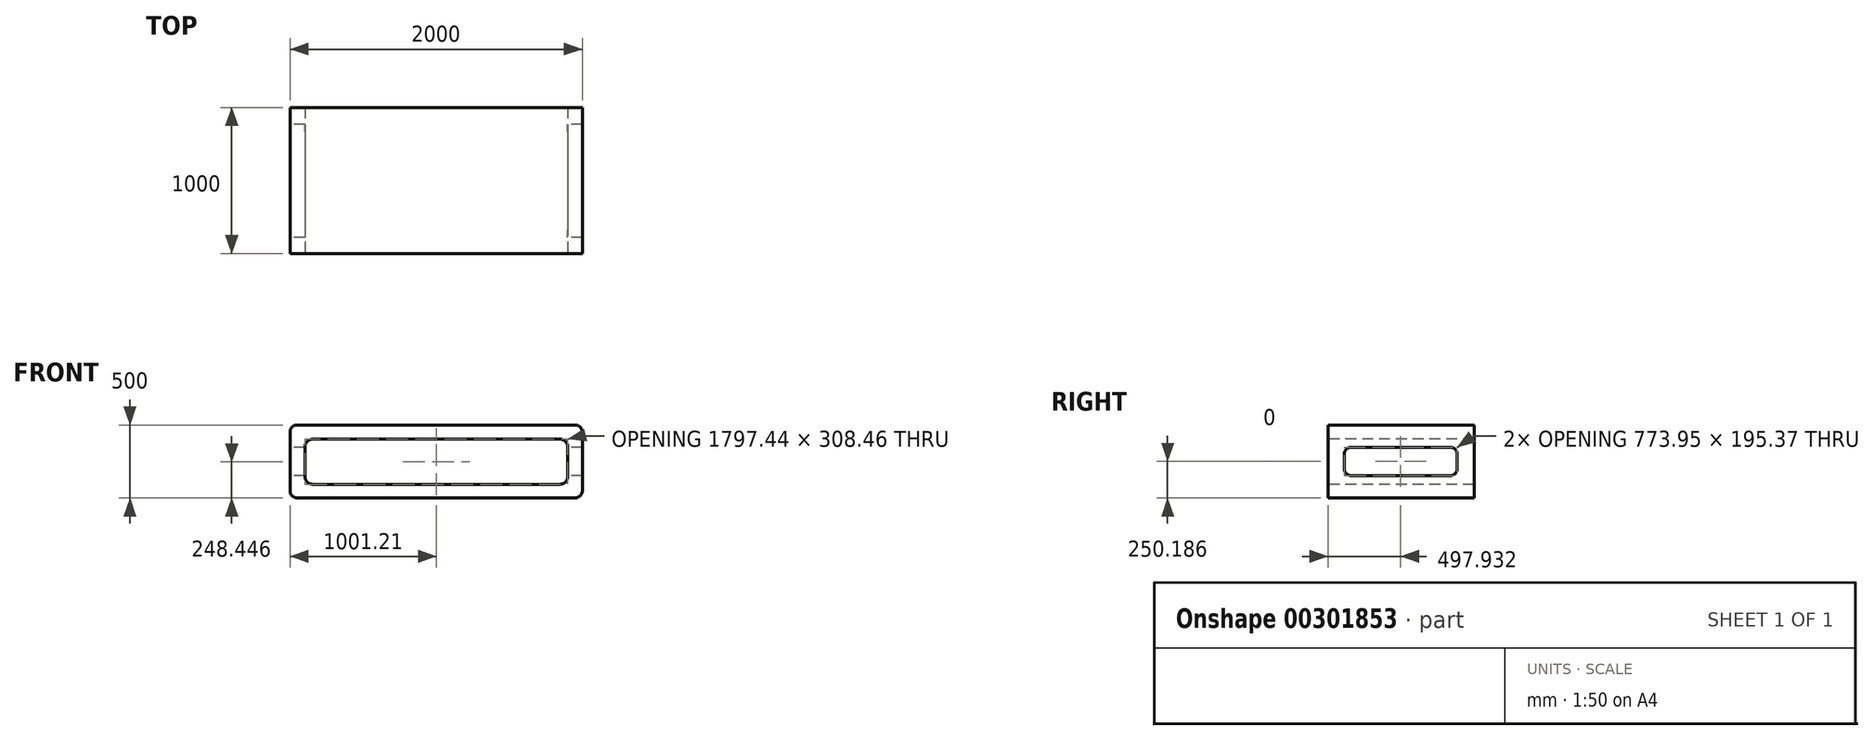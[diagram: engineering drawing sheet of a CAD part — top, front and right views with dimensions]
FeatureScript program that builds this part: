
annotation { "Feature Type Name" : "Feature", "Feature Type Description" : "" }
export const myFeature = defineFeature(function(context is Context, id is Id, definition is map)
    precondition{}
    {
        {
            var Q0;
            Q0=qCreatedBy(makeId("Front.planeOp"),FACE);
            var sketch = newSketch(context, id + "F0", { "sketchPlane" : qUnion([Q0])});
            skLineSegment(sketch, "E0.bottom", {"start": v(1000, 213.46) * mm, "end": v(-1000, 213.46) * mm});
            skLineSegment(sketch, "E0.top", {"start": v(1000, -286.54) * mm, "end": v(-1000, -286.54) * mm});
            skLineSegment(sketch, "E0.left", {"start": v(1000, 213.46) * mm, "end": v(1000, -286.54) * mm});
            skLineSegment(sketch, "E0.right", {"start": v(-1000, 213.46) * mm, "end": v(-1000, -286.54) * mm});
            skPoint(sketch, "E0.middle", {"position": v(0, -36.54) * mm});
            skSolve(sketch);
        }
        {
            var Q0;
            Q0 = qSketchRegion(id + "F0", true);
            extrude(context, id + "F1", {"entities" : qUnion([Q0]), "depth" : 1000 * mm});
        }
        {
            var Q0;
            Q0=makeQuery(id+"F1.opExtrude","CAP_FACE",FACE,{"disambiguationData":[OSD([sQuery(id+"F0.wireOp",EDGE,"E0.bottom"),sQuery(id+"F0.wireOp",EDGE,"E0.top"),sQuery(id+"F0.wireOp",EDGE,"E0.left"),sQuery(id+"F0.wireOp",EDGE,"E0.right")])],"isStart":false});
            var sketch = newSketch(context, id + "F2", { "sketchPlane" : qUnion([Q0])});
            skLineSegment(sketch, "E1.bottom", {"start": v(-897.51, 116.14) * mm, "end": v(899.93, 116.14) * mm});
            skLineSegment(sketch, "E1.top", {"start": v(-897.51, -192.33) * mm, "end": v(899.93, -192.33) * mm});
            skLineSegment(sketch, "E1.left", {"start": v(-897.51, 116.14) * mm, "end": v(-897.51, -192.33) * mm});
            skLineSegment(sketch, "E1.right", {"start": v(899.93, 116.14) * mm, "end": v(899.93, -192.33) * mm});
            skSolve(sketch);
        }
        {
            var Q0;
            Q0=makeQuery(id+"F2.imprint","IMPRINT",FACE,{"disambiguationData":[TD([[makeQuery(id+"F2.imprint","IMPRINT",EDGE,{"derivedFrom":sQuery(id+"F2.wireOp",EDGE,"E1.bottom")}),-1.0]])]});
            extrude(context, id + "F3", {"entities" : qUnion([Q0]), "operationType" : NewBodyOperationType.REMOVE, "endBound" : BoundingType.THROUGH_ALL, "oppositeDirection" : true, "depth" : 25 * mm});
        }
        {
            var Q0;
            Q0=makeQuery(id+"F1.opExtrude","SWEPT_EDGE",EDGE,{"disambiguationData":[OSD([sQuery(id+"F0.wireOp",EDGE,"E0.bottom"),sQuery(id+"F0.wireOp",EDGE,"E0.left")])]});
            var Q1;
            Q1=makeQuery(id+"F1.opExtrude","SWEPT_EDGE",EDGE,{"disambiguationData":[OSD([sQuery(id+"F0.wireOp",EDGE,"E0.top"),sQuery(id+"F0.wireOp",EDGE,"E0.left")])]});
            var Q2;
            Q2=makeQuery(id+"F1.opExtrude","SWEPT_EDGE",EDGE,{"disambiguationData":[OSD([sQuery(id+"F0.wireOp",EDGE,"E0.bottom"),sQuery(id+"F0.wireOp",EDGE,"E0.right")])]});
            var Q3;
            Q3=makeQuery(id+"F1.opExtrude","SWEPT_EDGE",EDGE,{"disambiguationData":[OSD([sQuery(id+"F0.wireOp",EDGE,"E0.top"),sQuery(id+"F0.wireOp",EDGE,"E0.right")])]});
            var Q4;
            Q4=makeQuery(id+"F3.boolean.opBoolean","COPY",EDGE,{"derivedFrom":makeQuery(id+"F3.opExtrude","SWEPT_EDGE",EDGE,{"disambiguationData":[OSD([sQuery(id+"F2.wireOp",EDGE,"E1.bottom"),sQuery(id+"F2.wireOp",EDGE,"E1.left")])]})});
            var Q5;
            Q5=makeQuery(id+"F3.boolean.opBoolean","COPY",EDGE,{"derivedFrom":makeQuery(id+"F3.opExtrude","SWEPT_EDGE",EDGE,{"disambiguationData":[OSD([sQuery(id+"F2.wireOp",EDGE,"E1.top"),sQuery(id+"F2.wireOp",EDGE,"E1.left")])]})});
            var Q6;
            Q6=makeQuery(id+"F3.boolean.opBoolean","COPY",EDGE,{"derivedFrom":makeQuery(id+"F3.opExtrude","SWEPT_EDGE",EDGE,{"disambiguationData":[OSD([sQuery(id+"F2.wireOp",EDGE,"E1.bottom"),sQuery(id+"F2.wireOp",EDGE,"E1.right")])]})});
            var Q7;
            Q7=makeQuery(id+"F3.boolean.opBoolean","COPY",EDGE,{"derivedFrom":makeQuery(id+"F3.opExtrude","SWEPT_EDGE",EDGE,{"disambiguationData":[OSD([sQuery(id+"F2.wireOp",EDGE,"E1.top"),sQuery(id+"F2.wireOp",EDGE,"E1.right")])]})});
            fillet(context, id + "F4", {"entities" : qUnion([Q0, Q1, Q2, Q3, Q4, Q5, Q6, Q7]), "radius" : 50 * mm, "tangentPropagation" : true, "allowEdgeOverflow" : false});
        }
        {
            var Q0;
            Q0=makeQuery(id+"F1.opExtrude","SWEPT_FACE",FACE,{"disambiguationData":[OSD([sQuery(id+"F0.wireOp",EDGE,"E0.right")])]});
            var sketch = newSketch(context, id + "F5", { "sketchPlane" : qUnion([Q0])});
            skLineSegment(sketch, "E2.bottom", {"start": v(115.1, 61.33) * mm, "end": v(889.04, 61.33) * mm});
            skLineSegment(sketch, "E2.top", {"start": v(115.1, -134.04) * mm, "end": v(889.04, -134.04) * mm});
            skLineSegment(sketch, "E2.left", {"start": v(115.1, 61.33) * mm, "end": v(115.1, -134.04) * mm});
            skLineSegment(sketch, "E2.right", {"start": v(889.04, 61.33) * mm, "end": v(889.04, -134.04) * mm});
            skSolve(sketch);
        }
        {
            var Q0;
            Q0=makeQuery(id+"F5.imprint","IMPRINT",FACE,{"disambiguationData":[TD([[makeQuery(id+"F5.imprint","IMPRINT",EDGE,{"derivedFrom":sQuery(id+"F5.wireOp",EDGE,"E2.bottom")}),-1.0]])]});
            extrude(context, id + "F6", {"entities" : qUnion([Q0]), "operationType" : NewBodyOperationType.REMOVE, "endBound" : BoundingType.THROUGH_ALL, "oppositeDirection" : true, "depth" : 25 * mm});
        }
        {
            var Q0;
            {var subQ0=sQuery(id+"F5.wireOp",EDGE,"E2.left");var subQ1=sQuery(id+"F5.wireOp",EDGE,"E2.bottom");Q0=makeQuery(id+"F6.boolean.opBoolean","COPY",EDGE,{"disambiguationData":[TD([makeQuery(id+"F1.opExtrude","SWEPT_FACE",FACE,{"disambiguationData":[OSD([sQuery(id+"F0.wireOp",EDGE,"E0.left")])]})])],"derivedFrom":makeQuery(id+"F6.opExtrude","SWEPT_EDGE",EDGE,{"disambiguationData":[OSD([subQ1,subQ0])]})});}
            var Q1;
            {var subQ0=sQuery(id+"F5.wireOp",EDGE,"E2.bottom");var subQ1=sQuery(id+"F5.wireOp",EDGE,"E2.right");Q1=makeQuery(id+"F6.boolean.opBoolean","COPY",EDGE,{"disambiguationData":[TD([makeQuery(id+"F1.opExtrude","SWEPT_FACE",FACE,{"disambiguationData":[OSD([sQuery(id+"F0.wireOp",EDGE,"E0.left")])]})])],"derivedFrom":makeQuery(id+"F6.opExtrude","SWEPT_EDGE",EDGE,{"disambiguationData":[OSD([subQ0,subQ1])]})});}
            var Q2;
            {var subQ0=sQuery(id+"F5.wireOp",EDGE,"E2.left");var subQ1=sQuery(id+"F5.wireOp",EDGE,"E2.top");Q2=makeQuery(id+"F6.boolean.opBoolean","COPY",EDGE,{"disambiguationData":[TD([makeQuery(id+"F1.opExtrude","SWEPT_FACE",FACE,{"disambiguationData":[OSD([sQuery(id+"F0.wireOp",EDGE,"E0.left")])]})])],"derivedFrom":makeQuery(id+"F6.opExtrude","SWEPT_EDGE",EDGE,{"disambiguationData":[OSD([subQ1,subQ0])]})});}
            var Q3;
            {var subQ0=sQuery(id+"F5.wireOp",EDGE,"E2.top");var subQ1=sQuery(id+"F5.wireOp",EDGE,"E2.right");Q3=makeQuery(id+"F6.boolean.opBoolean","COPY",EDGE,{"disambiguationData":[TD([makeQuery(id+"F1.opExtrude","SWEPT_FACE",FACE,{"disambiguationData":[OSD([sQuery(id+"F0.wireOp",EDGE,"E0.left")])]})])],"derivedFrom":makeQuery(id+"F6.opExtrude","SWEPT_EDGE",EDGE,{"disambiguationData":[OSD([subQ0,subQ1])]})});}
            var Q4;
            {var subQ0=sQuery(id+"F5.wireOp",EDGE,"E2.top");var subQ1=sQuery(id+"F5.wireOp",EDGE,"E2.right");Q4=makeQuery(id+"F6.boolean.opBoolean","COPY",EDGE,{"disambiguationData":[TD([makeQuery(id+"F1.opExtrude","SWEPT_FACE",FACE,{"disambiguationData":[OSD([sQuery(id+"F0.wireOp",EDGE,"E0.right")])]})])],"derivedFrom":makeQuery(id+"F6.opExtrude","SWEPT_EDGE",EDGE,{"disambiguationData":[OSD([subQ0,subQ1])]})});}
            var Q5;
            {var subQ0=sQuery(id+"F5.wireOp",EDGE,"E2.bottom");var subQ1=sQuery(id+"F5.wireOp",EDGE,"E2.right");Q5=makeQuery(id+"F6.boolean.opBoolean","COPY",EDGE,{"disambiguationData":[TD([makeQuery(id+"F1.opExtrude","SWEPT_FACE",FACE,{"disambiguationData":[OSD([sQuery(id+"F0.wireOp",EDGE,"E0.right")])]})])],"derivedFrom":makeQuery(id+"F6.opExtrude","SWEPT_EDGE",EDGE,{"disambiguationData":[OSD([subQ0,subQ1])]})});}
            var Q6;
            {var subQ0=sQuery(id+"F5.wireOp",EDGE,"E2.bottom");var subQ1=sQuery(id+"F5.wireOp",EDGE,"E2.left");Q6=makeQuery(id+"F6.boolean.opBoolean","COPY",EDGE,{"disambiguationData":[TD([makeQuery(id+"F1.opExtrude","SWEPT_FACE",FACE,{"disambiguationData":[OSD([sQuery(id+"F0.wireOp",EDGE,"E0.right")])]})])],"derivedFrom":makeQuery(id+"F6.opExtrude","SWEPT_EDGE",EDGE,{"disambiguationData":[OSD([subQ0,subQ1])]})});}
            var Q7;
            {var subQ0=sQuery(id+"F5.wireOp",EDGE,"E2.top");var subQ1=sQuery(id+"F5.wireOp",EDGE,"E2.left");Q7=makeQuery(id+"F6.boolean.opBoolean","COPY",EDGE,{"disambiguationData":[TD([makeQuery(id+"F1.opExtrude","SWEPT_FACE",FACE,{"disambiguationData":[OSD([sQuery(id+"F0.wireOp",EDGE,"E0.right")])]})])],"derivedFrom":makeQuery(id+"F6.opExtrude","SWEPT_EDGE",EDGE,{"disambiguationData":[OSD([subQ0,subQ1])]})});}
            fillet(context, id + "F7", {"entities" : qUnion([Q0, Q1, Q2, Q3, Q4, Q5, Q6, Q7]), "radius" : 50 * mm, "tangentPropagation" : true, "allowEdgeOverflow" : false});
        }
    });
